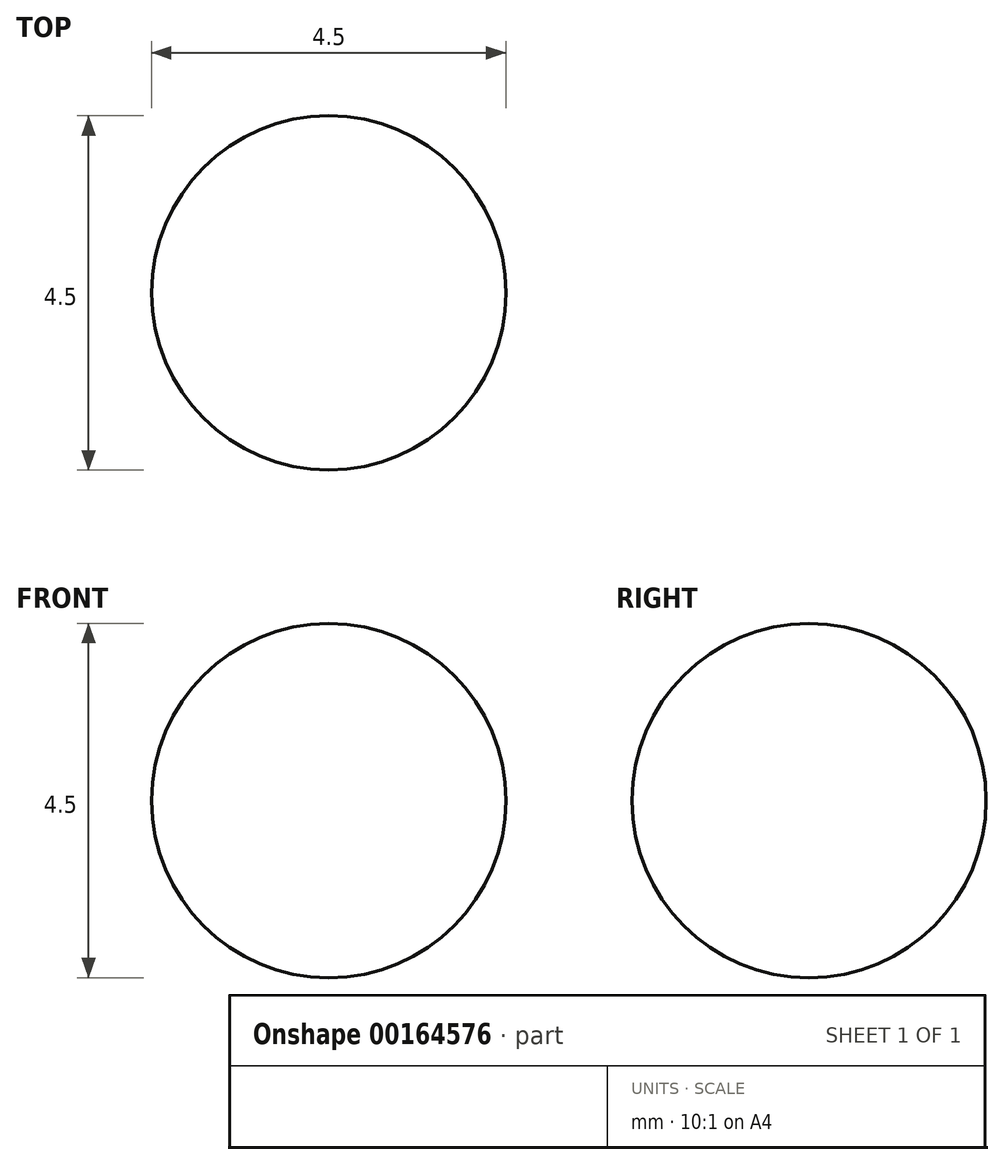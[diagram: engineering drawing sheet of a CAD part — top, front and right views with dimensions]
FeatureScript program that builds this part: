
annotation { "Feature Type Name" : "Feature", "Feature Type Description" : "" }
export const myFeature = defineFeature(function(context is Context, id is Id, definition is map)
    precondition{}
    {
        {
            var Q0;
            Q0=qCreatedBy(makeId("Top.planeOp"),FACE);
            var sketch = newSketch(context, id + "F0", { "sketchPlane" : qUnion([Q0])});
            skCircle(sketch, "E0", {"center": v(0, 0) * mm, "radius": 2.25 * mm});
            skLineSegment(sketch, "E1", {"start": v(0, 2.25) * mm, "end": v(0, -2.25) * mm});
            skSolve(sketch);
        }
        {
            var Q0;
            Q0=makeQuery(id+"F0.imprint","IMPRINT",FACE,{"disambiguationData":[TD([[makeQuery(id+"F0.imprint","IMPRINT",EDGE,{"derivedFrom":sQuery(id+"F0.wireOp",EDGE,"E0")}),1.0]])]});
            var sketch = newSketch(context, id + "F1", { "sketchPlane" : qUnion([Q0])});
            skCircle(sketch, "E2.0", {"center": v(0, 0) * mm, "radius": 2.25 * mm});
            skLineSegment(sketch, "E3", {"start": v(0, 2.25) * mm, "end": v(0, -2.25) * mm});
            skSolve(sketch);
        }
        {
            var Q0;
            {var subQ0=sQuery(id+"F0.wireOp",EDGE,"E1");Q0=makeQuery(id+"F0.imprint","IMPRINT",FACE,{"disambiguationData":[TD([[makeQuery(id+"F0.imprint","IMPRINT",EDGE,{"derivedFrom":subQ0}),-1.0]])]});}
            var Q1;
            Q1=sQuery(id+"F1.wireOp",EDGE,"E3");
            revolve(context, id + "F2", {"entities" : qUnion([Q0]), "axis" : qUnion([Q1]), "revolveType" : RevolveType.FULL});
        }
    });
